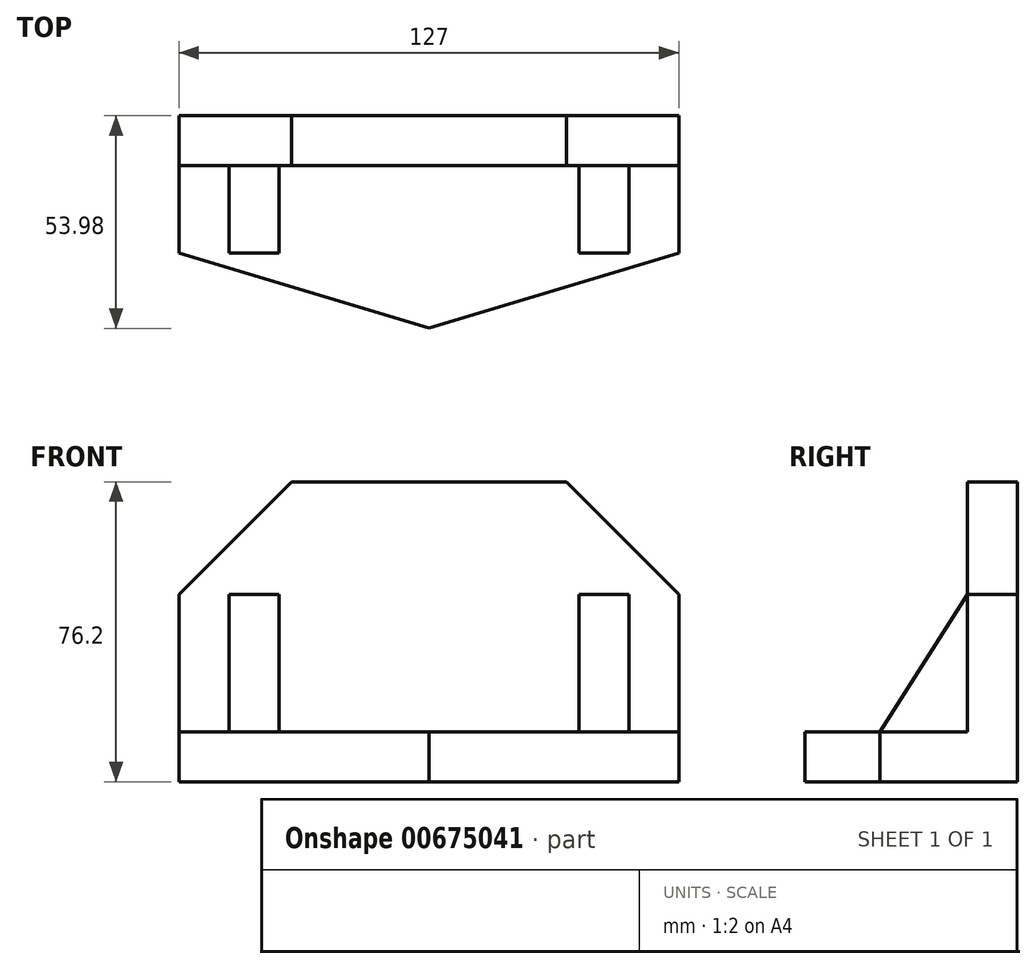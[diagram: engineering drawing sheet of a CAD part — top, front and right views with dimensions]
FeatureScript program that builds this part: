
annotation { "Feature Type Name" : "Feature", "Feature Type Description" : "" }
export const myFeature = defineFeature(function(context is Context, id is Id, definition is map)
    precondition{}
    {
        {
            var Q0;
            Q0=qCreatedBy(makeId("Front.planeOp"),FACE);
            var sketch = newSketch(context, id + "F0", { "sketchPlane" : qUnion([Q0])});
            skLineSegment(sketch, "E0", {"start": v(-83.32, 33.47) * mm, "end": v(-83.32, -14.15) * mm});
            skLineSegment(sketch, "E1", {"start": v(-83.32, -14.15) * mm, "end": v(43.68, -14.15) * mm});
            skLineSegment(sketch, "E2", {"start": v(43.68, -14.15) * mm, "end": v(43.68, 33.47) * mm});
            skLineSegment(sketch, "E3", {"start": v(43.68, 33.47) * mm, "end": v(15.1, 62.05) * mm});
            skLineSegment(sketch, "E4", {"start": v(15.1, 62.05) * mm, "end": v(-54.75, 62.05) * mm});
            skLineSegment(sketch, "E5", {"start": v(-54.75, 62.05) * mm, "end": v(-83.32, 33.47) * mm});
            skSolve(sketch);
        }
        {
            var Q0;
            Q0=makeQuery(id+"F0.imprint","IMPRINT",FACE,{"disambiguationData":[TD([[makeQuery(id+"F0.imprint","IMPRINT",EDGE,{"derivedFrom":sQuery(id+"F0.wireOp",EDGE,"E0")}),1.0]])]});
            extrude(context, id + "F1", {"entities" : qUnion([Q0]), "depth" : 12.7 * mm, "offsetDistance" : 25.4 * mm});
        }
        {
            var Q0;
            Q0=makeQuery(id+"F1.opExtrude","CAP_FACE",FACE,{"disambiguationData":[OSD([sQuery(id+"F0.wireOp",EDGE,"E0"),sQuery(id+"F0.wireOp",EDGE,"E1"),sQuery(id+"F0.wireOp",EDGE,"E2"),sQuery(id+"F0.wireOp",EDGE,"E3"),sQuery(id+"F0.wireOp",EDGE,"E4"),sQuery(id+"F0.wireOp",EDGE,"E5")])],"isStart":false});
            var sketch = newSketch(context, id + "F2", { "sketchPlane" : qUnion([Q0])});
            skLineSegment(sketch, "E6.bottom", {"start": v(-83.32, -14.15) * mm, "end": v(43.68, -14.15) * mm});
            skLineSegment(sketch, "E6.top", {"start": v(-83.32, -1.45) * mm, "end": v(43.68, -1.45) * mm});
            skLineSegment(sketch, "E6.left", {"start": v(-83.32, -14.15) * mm, "end": v(-83.32, -1.45) * mm});
            skLineSegment(sketch, "E6.right", {"start": v(43.68, -14.15) * mm, "end": v(43.68, -1.45) * mm});
            skSolve(sketch);
        }
        {
            var Q0;
            Q0=makeQuery(id+"F2.imprint","IMPRINT",FACE,{"disambiguationData":[TD([[makeQuery(id+"F2.imprint","IMPRINT",EDGE,{"derivedFrom":sQuery(id+"F2.wireOp",EDGE,"E6.bottom")}),1.0]])]});
            extrude(context, id + "F3", {"entities" : qUnion([Q0]), "operationType" : NewBodyOperationType.ADD, "depth" : 22.22 * mm, "offsetDistance" : 25.4 * mm});
        }
        {
            var Q0;
            Q0=makeQuery(id+"F3.opExtrude","SWEPT_FACE",FACE,{"disambiguationData":[OSD([sQuery(id+"F2.wireOp",EDGE,"E6.top")])]});
            var sketch = newSketch(context, id + "F4", { "sketchPlane" : qUnion([Q0])});
            skLineSegment(sketch, "E7", {"start": v(-83.32, -34.93) * mm, "end": v(-19.82, -53.98) * mm});
            skPoint(sketch, "E7.endSnap0", {"position": v(-19.82, -34.93) * mm});
            skLineSegment(sketch, "E8", {"start": v(-19.82, -53.98) * mm, "end": v(43.68, -34.93) * mm});
            skSolve(sketch);
        }
        {
            var Q0;
            Q0=makeQuery(id+"F4.imprint","IMPRINT",FACE,{"disambiguationData":[TD([[makeQuery(id+"F4.imprint","IMPRINT",EDGE,{"derivedFrom":sQuery(id+"F4.wireOp",EDGE,"E7")}),1.0]])]});
            extrude(context, id + "F5", {"entities" : qUnion([Q0]), "operationType" : NewBodyOperationType.ADD, "oppositeDirection" : true, "depth" : 12.7 * mm, "offsetDistance" : 25.4 * mm});
        }
        {
            var Q0;
            Q0=makeQuery(id+"F1.opExtrude","CAP_FACE",FACE,{"disambiguationData":[OSD([sQuery(id+"F0.wireOp",EDGE,"E0"),sQuery(id+"F0.wireOp",EDGE,"E1"),sQuery(id+"F0.wireOp",EDGE,"E2"),sQuery(id+"F0.wireOp",EDGE,"E3"),sQuery(id+"F0.wireOp",EDGE,"E4"),sQuery(id+"F0.wireOp",EDGE,"E5")])],"isStart":false});
            var sketch = newSketch(context, id + "F6", { "sketchPlane" : qUnion([Q0])});
            skLineSegment(sketch, "E9.bottom", {"start": v(-70.62, -1.45) * mm, "end": v(-57.92, -1.45) * mm});
            skLineSegment(sketch, "E9.top", {"start": v(-70.62, 33.47) * mm, "end": v(-57.92, 33.47) * mm});
            skLineSegment(sketch, "E9.left", {"start": v(-70.62, -1.45) * mm, "end": v(-70.62, 33.47) * mm});
            skLineSegment(sketch, "E9.right", {"start": v(-57.92, -1.45) * mm, "end": v(-57.92, 33.47) * mm});
            skLineSegment(sketch, "E10.bottom", {"start": v(30.98, -1.45) * mm, "end": v(18.28, -1.45) * mm});
            skLineSegment(sketch, "E10.top", {"start": v(30.98, 33.47) * mm, "end": v(18.28, 33.47) * mm});
            skLineSegment(sketch, "E10.left", {"start": v(30.98, -1.45) * mm, "end": v(30.98, 33.47) * mm});
            skLineSegment(sketch, "E10.right", {"start": v(18.28, -1.45) * mm, "end": v(18.28, 33.47) * mm});
            skSolve(sketch);
        }
        {
            var Q0;
            Q0=makeQuery(id+"F6.imprint","IMPRINT",FACE,{"disambiguationData":[TD([[makeQuery(id+"F6.imprint","IMPRINT",EDGE,{"derivedFrom":sQuery(id+"F6.wireOp",EDGE,"E9.bottom")}),1.0]])]});
            var Q1;
            Q1=makeQuery(id+"F6.imprint","IMPRINT",FACE,{"disambiguationData":[TD([[makeQuery(id+"F6.imprint","IMPRINT",EDGE,{"derivedFrom":sQuery(id+"F6.wireOp",EDGE,"E10.bottom")}),1.0]])]});
            extrude(context, id + "F7", {"entities" : qUnion([Q0, Q1]), "operationType" : NewBodyOperationType.ADD, "depth" : 22.22 * mm, "offsetDistance" : 25.4 * mm});
        }
        {
            var Q0;
            Q0=makeQuery(id+"F7.opExtrude","SWEPT_FACE",FACE,{"disambiguationData":[OSD([sQuery(id+"F6.wireOp",EDGE,"E10.left")])]});
            var sketch = newSketch(context, id + "F8", { "sketchPlane" : qUnion([Q0])});
            skLineSegment(sketch, "E11", {"start": v(-12.7, 33.47) * mm, "end": v(-34.93, -1.45) * mm});
            skSolve(sketch);
        }
        {
            var Q0;
            Q0=makeQuery(id+"F7.opExtrude","SWEPT_FACE",FACE,{"disambiguationData":[OSD([sQuery(id+"F6.wireOp",EDGE,"E9.right")])]});
            var sketch = newSketch(context, id + "F9", { "sketchPlane" : qUnion([Q0])});
            skLineSegment(sketch, "E12", {"start": v(-34.93, -1.45) * mm, "end": v(-12.7, 33.47) * mm});
            skSolve(sketch);
        }
        {
            var Q0;
            Q0=makeQuery(id+"F9.imprint","IMPRINT",FACE,{"disambiguationData":[TD([[makeQuery(id+"F9.imprint","IMPRINT",EDGE,{"derivedFrom":sQuery(id+"F9.wireOp",EDGE,"E12")}),1.0]])]});
            var Q1;
            Q1=makeQuery(id+"F8.imprint","IMPRINT",FACE,{"disambiguationData":[TD([[makeQuery(id+"F8.imprint","IMPRINT",EDGE,{"derivedFrom":sQuery(id+"F8.wireOp",EDGE,"E11")}),-1.0]])]});
            extrude(context, id + "F10", {"entities" : qUnion([Q0, Q1]), "operationType" : NewBodyOperationType.REMOVE, "endBound" : BoundingType.THROUGH_ALL, "oppositeDirection" : true, "depth" : 25.4 * mm, "offsetDistance" : 25.4 * mm});
        }
    });
